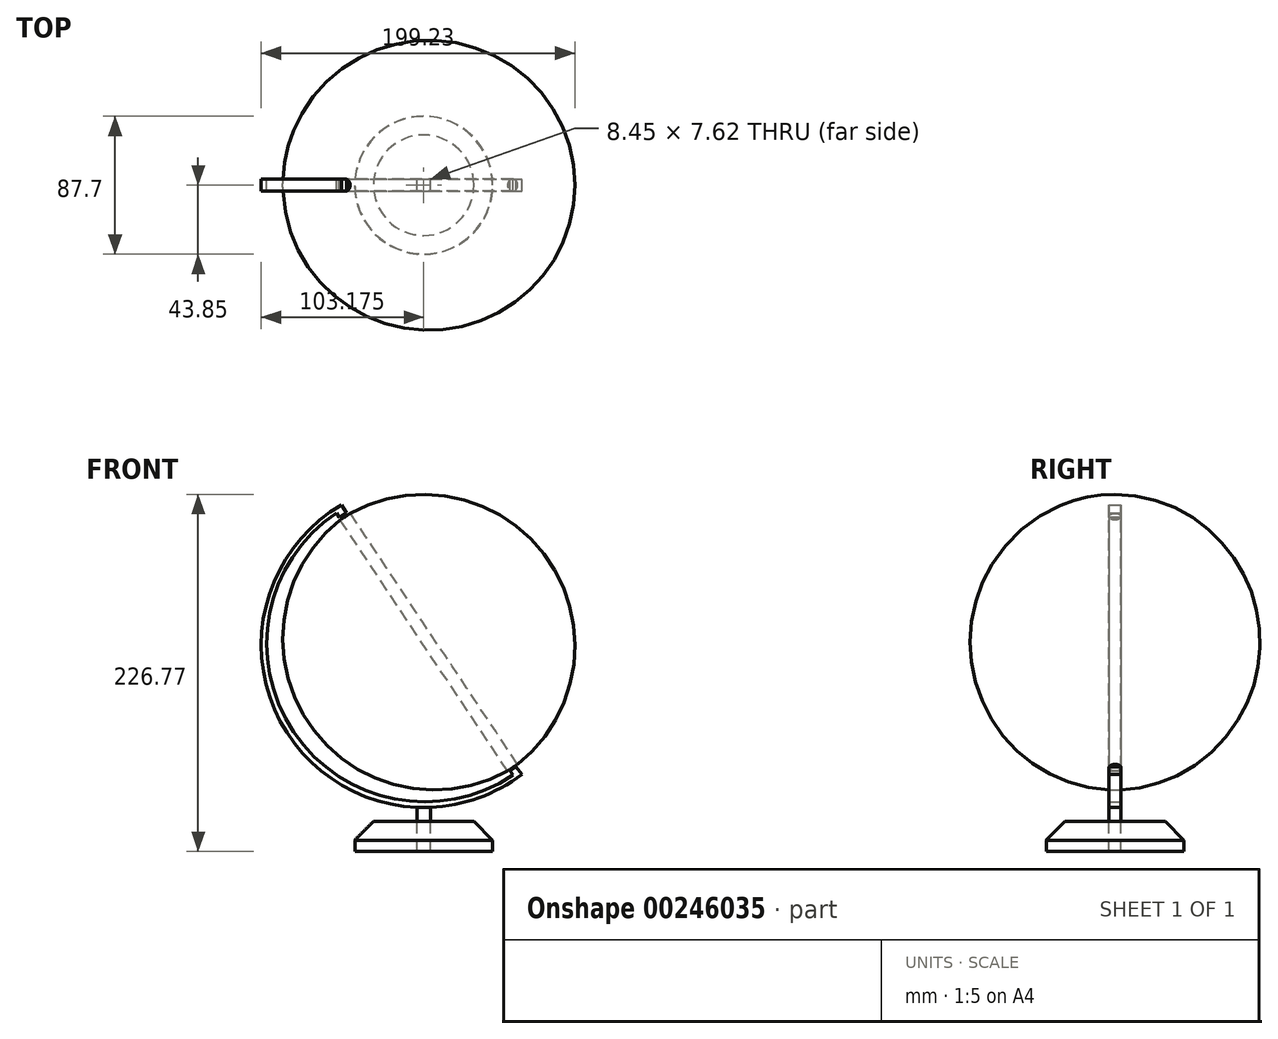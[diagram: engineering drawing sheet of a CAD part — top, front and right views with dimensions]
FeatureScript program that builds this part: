
annotation { "Feature Type Name" : "Feature", "Feature Type Description" : "" }
export const myFeature = defineFeature(function(context is Context, id is Id, definition is map)
    precondition{}
    {
        {
            var Q0;
            Q0=qCreatedBy(makeId("Front.planeOp"),FACE);
            var sketch = newSketch(context, id + "F0", { "sketchPlane" : qUnion([Q0])});
            skLineSegment(sketch, "E0", {"start": v(52.1, -76.92) * mm, "end": v(55.38, -74.4) * mm});
            skLineSegment(sketch, "E1", {"start": v(-51.15, 85.02) * mm, "end": v(-54.58, 82.73) * mm});
            skLineSegment(sketch, "E2", {"start": v(-54.58, 82.73) * mm, "end": v(52.1, -76.92) * mm});
            skLineSegment(sketch, "E3", {"start": v(55.38, -74.4) * mm, "end": v(-51.15, 85.02) * mm});
            skLineSegment(sketch, "E4", {"start": v(-45.54, 85.9) * mm, "end": v(57.7, -68.6) * mm});
            skArc(sketch, "E5", {"start": v(57.7, -68.6) * mm, "mid": v(72.77, 53.21) * mm, "end": v(-45.54, 85.9) * mm});
            skPoint(sketch, "E6", {"position": v(66.92, 61.05) * mm});
            skSolve(sketch);
        }
        {
            var Q0;
            Q0=sQuery(id+"F0.wireOp",EDGE,"E2");
            var Q1;
            Q1=sQuery(id+"F0.wireOp",EDGE,"E3");
            revolve(context, id + "F1", {"bodyType" : ToolBodyType.SURFACE, "surfaceEntities" : qUnion([Q0]), "axis" : qUnion([Q1]), "revolveType" : RevolveType.FULL});
        }
        {
            var Q0;
            Q0=qCreatedBy(makeId("Front.planeOp"),FACE);
            var sketch = newSketch(context, id + "F2", { "sketchPlane" : qUnion([Q0])});
            skLineSegment(sketch, "E7", {"start": v(56.26, -75.22) * mm, "end": v(58.23, -73.72) * mm});
            skLineSegment(sketch, "E8", {"start": v(58.23, -73.72) * mm, "end": v(-49.83, 87.8) * mm});
            skLineSegment(sketch, "E9", {"start": v(-49.83, 87.8) * mm, "end": v(-52.14, 86.26) * mm});
            skLineSegment(sketch, "E10", {"start": v(-52.14, 86.26) * mm, "end": v(56.26, -75.22) * mm});
            skSolve(sketch);
        }
        {
            var Q0;
            Q0=sQuery(id+"F2.wireOp",EDGE,"E8");
            var Q1;
            Q1=sQuery(id+"F2.wireOp",EDGE,"E7");
            var Q2;
            Q2=sQuery(id+"F2.wireOp",EDGE,"E9");
            var Q3;
            Q3=sQuery(id+"F2.wireOp",EDGE,"E10");
            revolve(context, id + "F3", {"bodyType" : ToolBodyType.SURFACE, "surfaceEntities" : qUnion([Q0, Q1, Q2]), "axis" : qUnion([Q3]), "revolveType" : RevolveType.FULL});
        }
        {
            var Q0;
            Q0=qCreatedBy(makeId("Front.planeOp"),FACE);
            var sketch = newSketch(context, id + "F4", { "sketchPlane" : qUnion([Q0])});
            skLineSegment(sketch, "E11", {"start": v(-47.5, 87.3) * mm, "end": v(58.88, -72.16) * mm});
            skLineSegment(sketch, "E12", {"start": v(-50.73, 85.22) * mm, "end": v(55.7, -74.33) * mm, "construction": true});
            skArc(sketch, "E13", {"start": v(58.88, -72.16) * mm, "mid": v(79.1, 56.53) * mm, "end": v(-47.5, 87.3) * mm});
            skSolve(sketch);
        }
        {
            var Q0;
            Q0=makeQuery(id+"F4.imprint","IMPRINT",FACE,{"disambiguationData":[TD([[makeQuery(id+"F4.imprint","IMPRINT",EDGE,{"derivedFrom":sQuery(id+"F4.wireOp",EDGE,"E11")}),1.0]])]});
            var Q1;
            Q1=sQuery(id+"F4.wireOp",EDGE,"E12");
            revolve(context, id + "F5", {"entities" : qUnion([Q0]), "axis" : qUnion([Q1]), "revolveType" : RevolveType.FULL});
        }
        {
            var Q0;
            Q0=qCreatedBy(makeId("Front.planeOp"),FACE);
            var sketch = newSketch(context, id + "F6", { "sketchPlane" : qUnion([Q0])});
            skLineSegment(sketch, "E14", {"start": v(-49.74, 87.63) * mm, "end": v(-52.98, 92.64) * mm});
            skLineSegment(sketch, "E15", {"start": v(-54.44, 84.96) * mm, "end": v(-56.17, 87.63) * mm});
            skLineSegment(sketch, "E16", {"start": v(58, -73.8) * mm, "end": v(61.67, -78.52) * mm});
            skLineSegment(sketch, "E17", {"start": v(54.13, -76.31) * mm, "end": v(58, -73.8) * mm});
            skArc(sketch, "E18", {"start": v(-52.98, 92.64) * mm, "mid": v(-86.52, -53.8) * mm, "end": v(61.67, -78.52) * mm});
            skLineSegment(sketch, "E19", {"start": v(54.13, -76.31) * mm, "end": v(56.04, -78.85) * mm});
            skArc(sketch, "E20", {"start": v(-56.17, 87.63) * mm, "mid": v(-83.3, -51.72) * mm, "end": v(56.04, -78.85) * mm});
            skLineSegment(sketch, "E21", {"start": v(-54.44, 84.96) * mm, "end": v(-54.15, 84.52) * mm});
            skLineSegment(sketch, "E22", {"start": v(-54.15, 84.52) * mm, "end": v(-49.74, 87.63) * mm});
            skLineSegment(sketch, "E23.bottom", {"start": v(-5.02, -99.48) * mm, "end": v(3.43, -99.48) * mm});
            skLineSegment(sketch, "E23.top", {"start": v(-5.02, -108.39) * mm, "end": v(3.43, -108.39) * mm});
            skLineSegment(sketch, "E23.left", {"start": v(-5.02, -99.48) * mm, "end": v(-5.02, -108.39) * mm});
            skLineSegment(sketch, "E23.right", {"start": v(3.43, -99.48) * mm, "end": v(3.43, -108.39) * mm});
            skSolve(sketch);
        }
        {
            var Q0;
            {var subQ4=sQuery(id+"F6.wireOp",EDGE,"E14");Q0=makeQuery(id+"F6.imprint","IMPRINT",FACE,{"disambiguationData":[TD([[makeQuery(id+"F6.imprint","IMPRINT",EDGE,{"derivedFrom":subQ4}),1.0]])]});}
            var Q1;
            {var subQ4=sQuery(id+"F6.wireOp",EDGE,"E23.top");Q1=makeQuery(id+"F6.imprint","IMPRINT",FACE,{"disambiguationData":[TD([[makeQuery(id+"F6.imprint","IMPRINT",EDGE,{"derivedFrom":subQ4}),1.0]])]});}
            extrude(context, id + "F7", {"entities" : qUnion([Q0, Q1]), "depth" : 3.8 * mm, "hasSecondDirection" : true, "secondDirectionOppositeDirection" : true, "secondDirectionDepth" : 3.8 * mm});
        }
        {
            var Q0;
            Q0=makeQuery(id+"F7.opExtrude","SWEPT_FACE",FACE,{"disambiguationData":[OSD([sQuery(id+"F6.wireOp",EDGE,"E23.top")])]});
            var sketch = newSketch(context, id + "F8", { "sketchPlane" : qUnion([Q0])});
            skCircle(sketch, "E24", {"center": v(-0.8, 0) * mm, "radius": 57.31 * mm});
            skPoint(sketch, "E24.centerSnap0", {"position": v(-0.8, -3.81) * mm});
            skSolve(sketch);
        }
        {
            var Q0;
            Q0=makeQuery(id+"F8.imprint","IMPRINT",FACE,{"disambiguationData":[TD([[makeQuery(id+"F8.imprint","IMPRINT",EDGE,{"derivedFrom":sQuery(id+"F8.wireOp",EDGE,"E24")}),1.0]])]});
            extrude(context, id + "F9", {"entities" : qUnion([Q0]), "depth" : 11.94 * mm});
        }
        {
            var Q0;
            Q0=makeQuery(id+"F9.opExtrude","CAP_EDGE",EDGE,{"disambiguationData":[OSD([sQuery(id+"F8.wireOp",EDGE,"E24")])],"isStart":true});
            chamfer(context, id + "F10", {"entities" : qUnion([Q0]), "width" : 25.4 * mm, "tangentPropagation" : true});
        }
        {
            var Q0;
            Q0=makeQuery(id+"F9.opExtrude","CAP_FACE",FACE,{"disambiguationData":[OSD([sQuery(id+"F6.wireOp",EDGE,"E23.top"),sQuery(id+"F6.wireOp",EDGE,"E23.left"),sQuery(id+"F6.wireOp",EDGE,"E23.right"),sQuery(id+"F8.wireOp",EDGE,"E24")])],"isStart":false});
            var sketch = newSketch(context, id + "F11", { "sketchPlane" : qUnion([Q0])});
            skCircle(sketch, "E25", {"center": v(-0.8, 0) * mm, "radius": 43.7 * mm});
            skSolve(sketch);
        }
        {
            var Q0;
            Q0=makeQuery(id+"F11.imprint","IMPRINT",FACE,{"disambiguationData":[TD([[makeQuery(id+"F11.imprint","IMPRINT",EDGE,{"derivedFrom":sQuery(id+"F11.wireOp",EDGE,"E25")}),1.0]])]});
            extrude(context, id + "F12", {"entities" : qUnion([Q0]), "operationType" : NewBodyOperationType.ADD, "depth" : 7.11 * mm});
        }
    });
